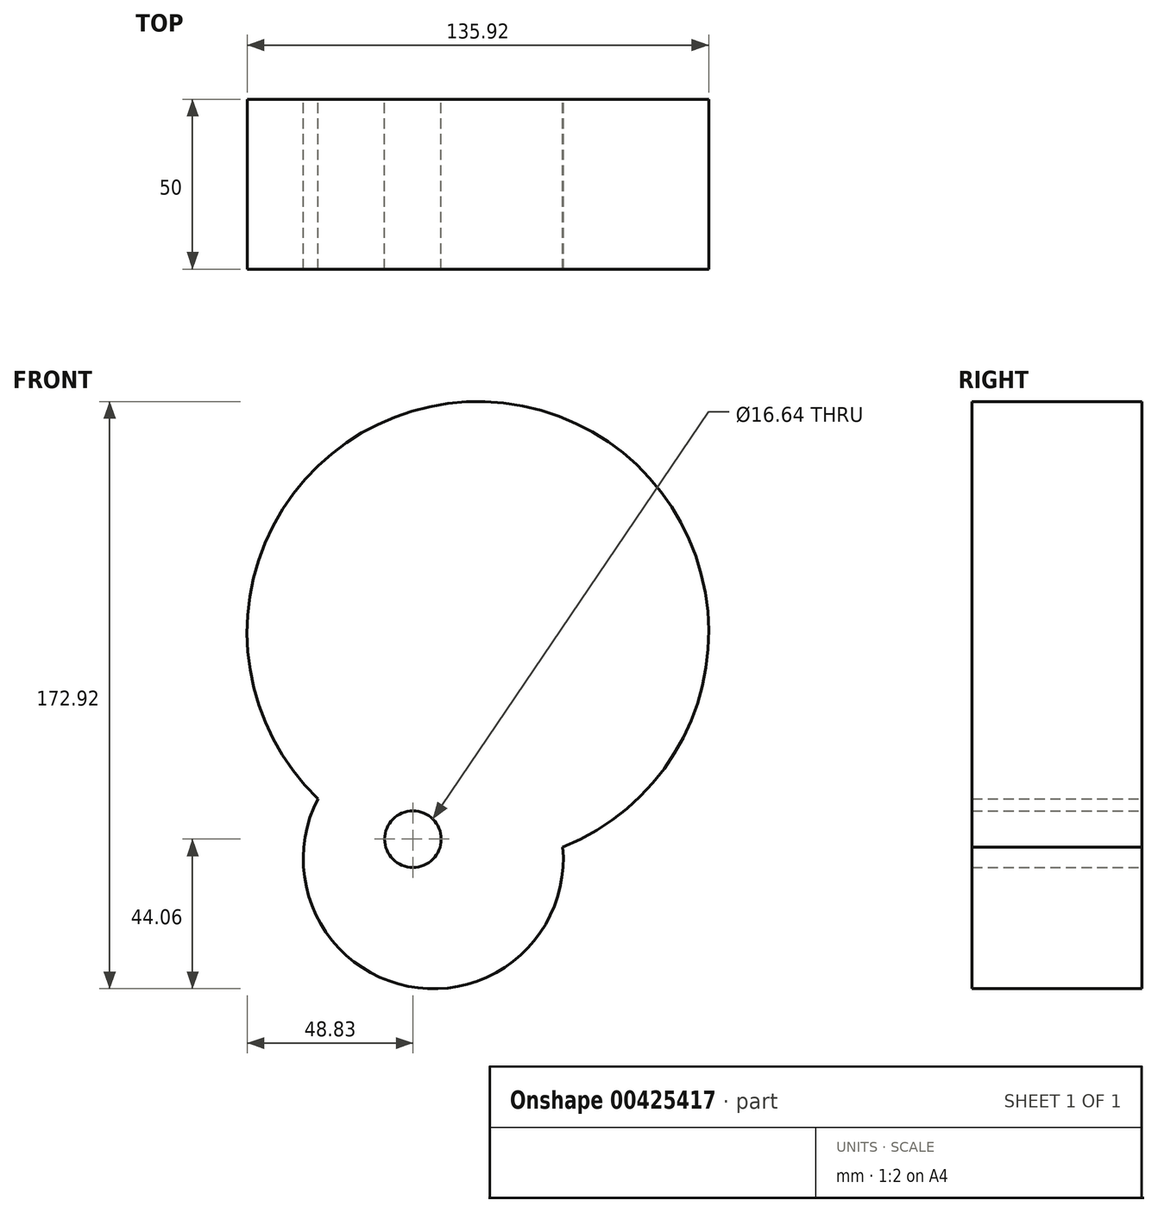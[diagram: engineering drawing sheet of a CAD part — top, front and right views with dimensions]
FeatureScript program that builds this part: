
annotation { "Feature Type Name" : "Feature", "Feature Type Description" : "" }
export const myFeature = defineFeature(function(context is Context, id is Id, definition is map)
    precondition{}
    {
        {
            var Q0;
            Q0=qCreatedBy(makeId("Front.planeOp"),FACE);
            var sketch = newSketch(context, id + "F0", { "sketchPlane" : qUnion([Q0])});
            skCircle(sketch, "E0", {"center": v(19.13, 60.9) * mm, "radius": 67.96 * mm});
            skCircle(sketch, "E1", {"center": v(0, 0) * mm, "radius": 5.4 * mm});
            skCircle(sketch, "E2", {"center": v(5.99, -5.78) * mm, "radius": 38.28 * mm});
            skCircle(sketch, "E3", {"center": v(0, 0) * mm, "radius": 8.32 * mm});
            skSolve(sketch);
        }
        {
            var Q0;
            Q0 = qSketchRegion(id + "F0", true);
            extrude(context, id + "F1", {"entities" : qUnion([Q0]), "flatOperationType" : FlatOperationType.REMOVE, "offsetDistance" : 25 * mm, "depth" : 50 * mm, "domain" : OperationDomain.MODEL});
        }
    });
